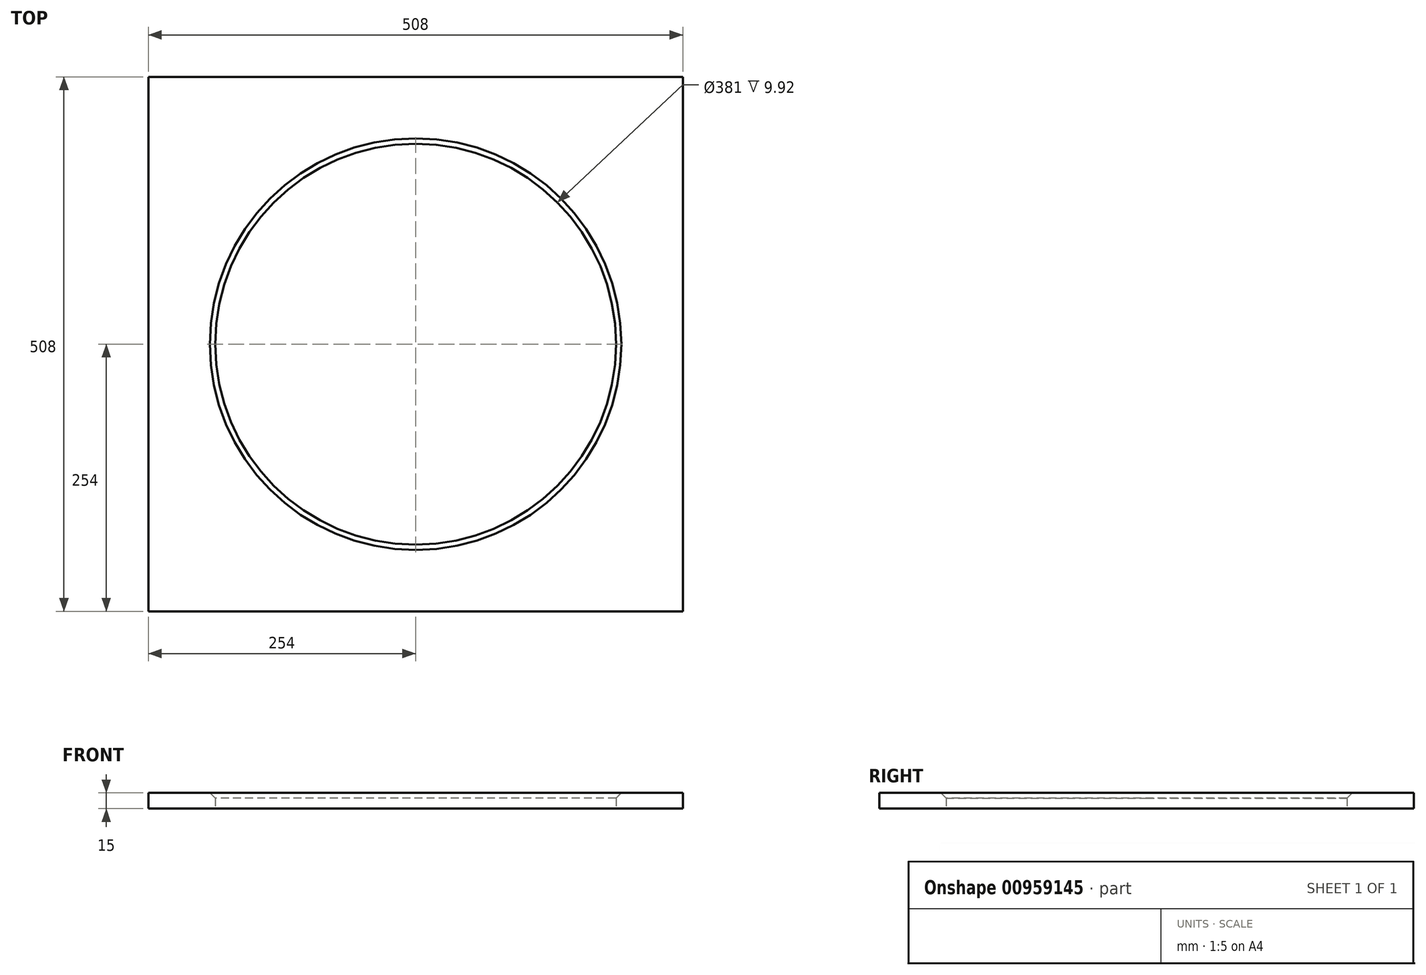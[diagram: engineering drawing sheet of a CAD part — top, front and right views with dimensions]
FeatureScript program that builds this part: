
annotation { "Feature Type Name" : "Feature", "Feature Type Description" : "" }
export const myFeature = defineFeature(function(context is Context, id is Id, definition is map)
    precondition{}
    {
        {
            var Q0;
            Q0=qCreatedBy(makeId("Top.planeOp"),FACE);
            var sketch = newSketch(context, id + "F0", { "sketchPlane" : qUnion([Q0])});
            skLineSegment(sketch, "E0.bottom", {"start": v(254, 254) * mm, "end": v(-254, 254) * mm});
            skLineSegment(sketch, "E0.top", {"start": v(254, -254) * mm, "end": v(-254, -254) * mm});
            skLineSegment(sketch, "E0.left", {"start": v(254, 254) * mm, "end": v(254, -254) * mm});
            skLineSegment(sketch, "E0.right", {"start": v(-254, 254) * mm, "end": v(-254, -254) * mm});
            skPoint(sketch, "E0.middle", {"position": v(0, 0) * mm});
            skCircle(sketch, "E1", {"center": v(0, 0) * mm, "radius": 190.5 * mm});
            skSolve(sketch);
        }
        {
            var Q0;
            Q0=makeQuery(id+"F0.imprint","IMPRINT",FACE,{"disambiguationData":[TD([[makeQuery(id+"F0.imprint","IMPRINT",EDGE,{"derivedFrom":sQuery(id+"F0.wireOp",EDGE,"E0.bottom")}),1.0]])]});
            extrude(context, id + "F1", {"entities" : qUnion([Q0]), "depth" : 15 * mm, "offsetDistance" : 25.4 * mm});
        }
        {
            var Q0;
            Q0=makeQuery(id+"F1.opExtrude","CAP_EDGE",EDGE,{"disambiguationData":[OSD([sQuery(id+"F0.wireOp",EDGE,"E1")])],"isStart":false});
            chamfer(context, id + "F2", {"entities" : qUnion([Q0]), "width" : 5.08 * mm, "tangentPropagation" : true});
        }
    });
